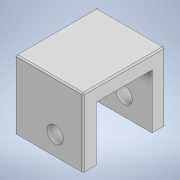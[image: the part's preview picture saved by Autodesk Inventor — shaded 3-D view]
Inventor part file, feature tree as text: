
AUTODESK INVENTOR PART (.ipt)
format: ipt  version: 2021.4 (Build 254397000, 397)  size: 140,800 bytes
history: native  units: mm
features: sketch x4, extrude x3, other x1, hole x1, fillet x1
ambient origin geometry x8: Origin, YZ Plane, XZ Plane, XY Plane, X Axis, Y Axis, Z Axis, Center Point
bodies: Body1 (feature_tree)
feature tree (10):
  other  "ソリッド1"
  extrude  "押し出し1"  Depth=25.0mm
  extrude  "押し出し2"  Depth=30.0mm
  hole  "穴1"  [1 undecoded]
  fillet  "フィレット1"  Radius=20.5mm
  extrude  "押し出し4"  Depth=20.5mm
  sketch  "スケッチ1"
  sketch  "スケッチ2"
  sketch  "スケッチ4"
  sketch  "スケッチ5"
note: 1 required parameter value undecoded (feature->parameter linkage not recoverable at this tier; creation-order binding heuristic only, values carry confidence <= 0.55)
